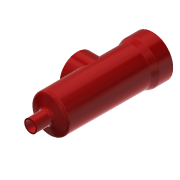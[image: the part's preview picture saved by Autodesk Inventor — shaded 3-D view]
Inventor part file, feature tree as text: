
AUTODESK INVENTOR PART (.ipt)
format: ipt  version: 2019.4 (Build 234330000, 330)  size: 225,792 bytes
history: native  units: mm
features: sketch x5, extrude x4, other x3, fillet x2, reference x2, revolve x1, projected_geometry x1
ambient origin geometry x8: Origin, YZ Plane, XZ Plane, XY Plane, X Axis, Y Axis, Z Axis, Center Point
bodies: Solid1 (feature_tree)
feature tree (18):
  revolve  "Revolution1"  [1 undecoded]
  extrude  "Extrusion3"  Depth=13.0mm
  extrude  "Extrusion4"  Depth=10.0mm
  sketch  "Sketch7"  dims[d21=6.4mm d22=10.0mm d23=0.0mm]
  fillet  "Fillet2"  Radius=10.0mm
  extrude  "Extrusion2"  Depth=10.0mm TaperAngle=0.0deg
  extrude  "Extrusion5"  Depth=65.0mm
  fillet  "Fillet3"  Radius=0.3mm
  sketch  "Sketch1"  dims[d6=90.0deg d12=4.0mm]
  reference  "Reference1"
  sketch  "Sketch4"  dims[d13=0.0mm d15=13.0mm]
  reference  "Reference2"
  projected_geometry  "Projected Loop2"
  sketch  "Sketch5"  dims[d17=2.0mm d19=5.0mm d20=10.0mm]
  sketch  "Sketch8"  dims[d24=2.0mm d25=65.0mm d26=0.3mm d27=15.0mm d28=0.0mm d29=15.0mm d30=-0.698132mm d31=2.0mm d32=65.0mm d33=-0.349066mm]
  other  "Assemlby_OpenOxygen.iam"
  other  "00_Sensirion_Flowsensor:1"
  other  "01_Connector_T:1"
note: 1 required parameter value undecoded (feature->parameter linkage not recoverable at this tier; creation-order binding heuristic only, values carry confidence <= 0.55)
